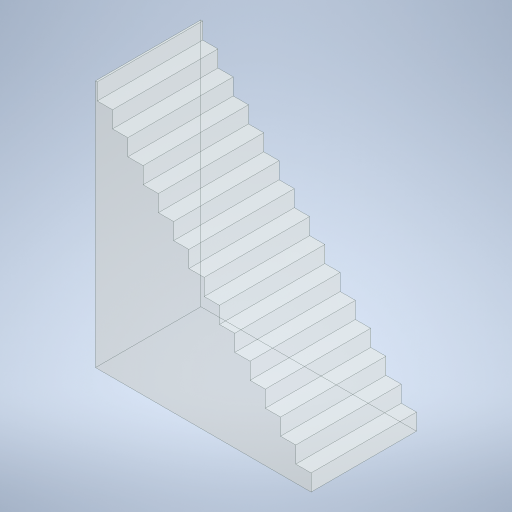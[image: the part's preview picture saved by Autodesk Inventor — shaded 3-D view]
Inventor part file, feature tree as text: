
AUTODESK INVENTOR PART (.ipt)
format: ipt  version: 2024 (Build 280153000, 153)  size: 325,120 bytes
history: native  units: in
note: dims shown in document units (in); Inventor stores cm internally (conversion verified against a paired STEP export)
features: extrude x1, sketch x1
ambient origin geometry x8: Origin, YZ Plane, XZ Plane, XY Plane, X Axis, Y Axis, Z Axis, Center Point
bodies: Solid1 (feature_tree)
feature tree (2):
  extrude  "Extrusion1"  Depth=104.25in
  sketch  "Sketch1"  dims[d4=44.25in d5=0.0in d21=104.25in d22=90.5in d23=0.75in]
